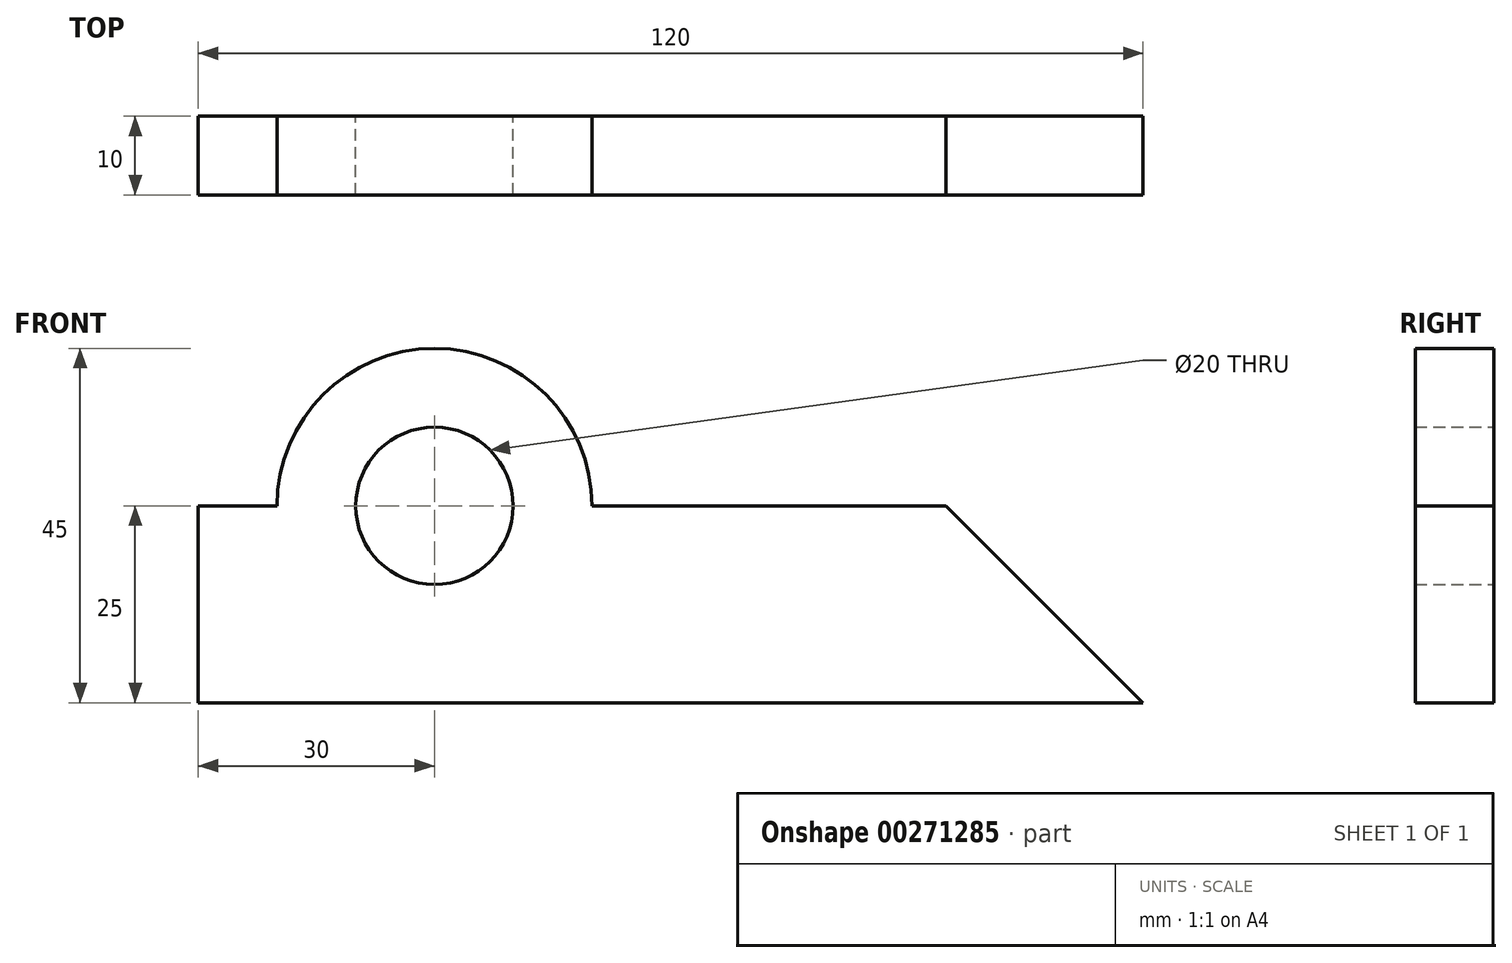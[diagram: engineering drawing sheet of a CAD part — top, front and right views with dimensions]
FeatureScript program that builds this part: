
annotation { "Feature Type Name" : "Feature", "Feature Type Description" : "" }
export const myFeature = defineFeature(function(context is Context, id is Id, definition is map)
    precondition{}
    {
        {
            var Q0;
            Q0=qCreatedBy(makeId("Front.planeOp"),FACE);
            var sketch = newSketch(context, id + "F0", { "sketchPlane" : qUnion([Q0])});
            skLineSegment(sketch, "E0", {"start": v(0, 0) * mm, "end": v(120, 0) * mm});
            skLineSegment(sketch, "E1", {"start": v(120, 0) * mm, "end": v(95, 25) * mm});
            skLineSegment(sketch, "E2", {"start": v(95, 25) * mm, "end": v(50, 25) * mm});
            skLineSegment(sketch, "E3", {"start": v(0, 0) * mm, "end": v(0, 25) * mm});
            skLineSegment(sketch, "E4", {"start": v(0, 25) * mm, "end": v(10, 25) * mm});
            skCircle(sketch, "E5", {"center": v(30, 25) * mm, "radius": 10 * mm});
            skArc(sketch, "E6", {"start": v(50, 25) * mm, "mid": v(30, 45) * mm, "end": v(10, 25) * mm});
            skSolve(sketch);
        }
        {
            var Q0;
            Q0=makeQuery(id+"F0.imprint","IMPRINT",FACE,{"disambiguationData":[TD([[makeQuery(id+"F0.imprint","IMPRINT",EDGE,{"derivedFrom":sQuery(id+"F0.wireOp",EDGE,"E0")}),1.0]])]});
            extrude(context, id + "F1", {"entities" : qUnion([Q0]), "depth" : 10 * mm});
        }
    });
